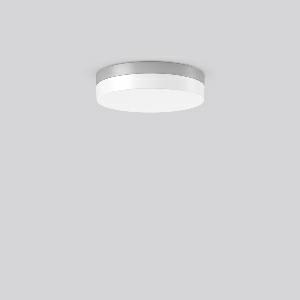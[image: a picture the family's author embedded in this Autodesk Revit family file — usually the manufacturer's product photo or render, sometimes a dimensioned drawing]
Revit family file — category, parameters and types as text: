
# Revit family: flat_slim_round_312630_004_19_2d02
name_source: partatom
category: Lighting Fixtures
units: mm (PartAtom-declared; Revit-internal decimal feet)

## family parameters
Cut with Voids When Loaded = No
Host = Face
Light Source = No
Part Type = Normal
Room Calculation Point = No
Round Connector Dimension = Use Diameter
Shared = No

## types (1)
- MultiLumen 1 830 (1 x LED Modul 830, 1300 lm, 3000)
    Apparent Load = 11 VA
    CIE Flux Codes = 39 70 89 83 100
    Color Rendering = 80
    Color Temperature = 3000
    Default Elevation = 1800 mm
    Height = 70 mm
    Lamp = 1 x LED Modul 830
    Lamp Light Flux = 1300 lm
    Lamp count = 1
    Length = 300 mm
    Lifetime = 50000 h
    Luminous efficacy = 118 lm/W
    Manufacturer = RZB
    ModVariant = No
    Model = 312630.004.19
    Mounting Place = Ceiling
    Mounting Type = Surface mounted
    Number of Poles = 1
    OnlyDefault = Yes
    Power Factor = 1
    Product Name = FLAT SLIM round
    Product group = Surface mounted ceiling and wall luminaires
    ProductGroupID = 305
    Protection Class = Protection class I
    Protection Degree = Degree of protection
    RLX_Detail_Level = 1
    RLX_Emergency_Light_Flux = 0 lm
    RLX_Emergency_Type = 0
    RLX_Emergency_Type_DB = No
    RlxData = <blob elided: 17281 chars, md5=d1cc5224>
    Socket = socket
    Standby Power = 0 W
    System Light Flux = 1300 lm
    System Power = 11 W
    Type Comments = MultiLumen 1 830
    Type Image = 312629.004.jpg
    URL = http://relux.com
    VarID = multilumen_1_830
    Voltage = 0 V
    Weight = 0.00 kg
    Width = 0 mm  [stored 0 ft]

note: [stored X ft] marks values corroborated as IEEE doubles in the binary element streams (Revit-internal decimal feet)

## geometry (parser evidence)
native form markers: Blend x4, Sweep x13
no freeform markers — native parametric forms only
